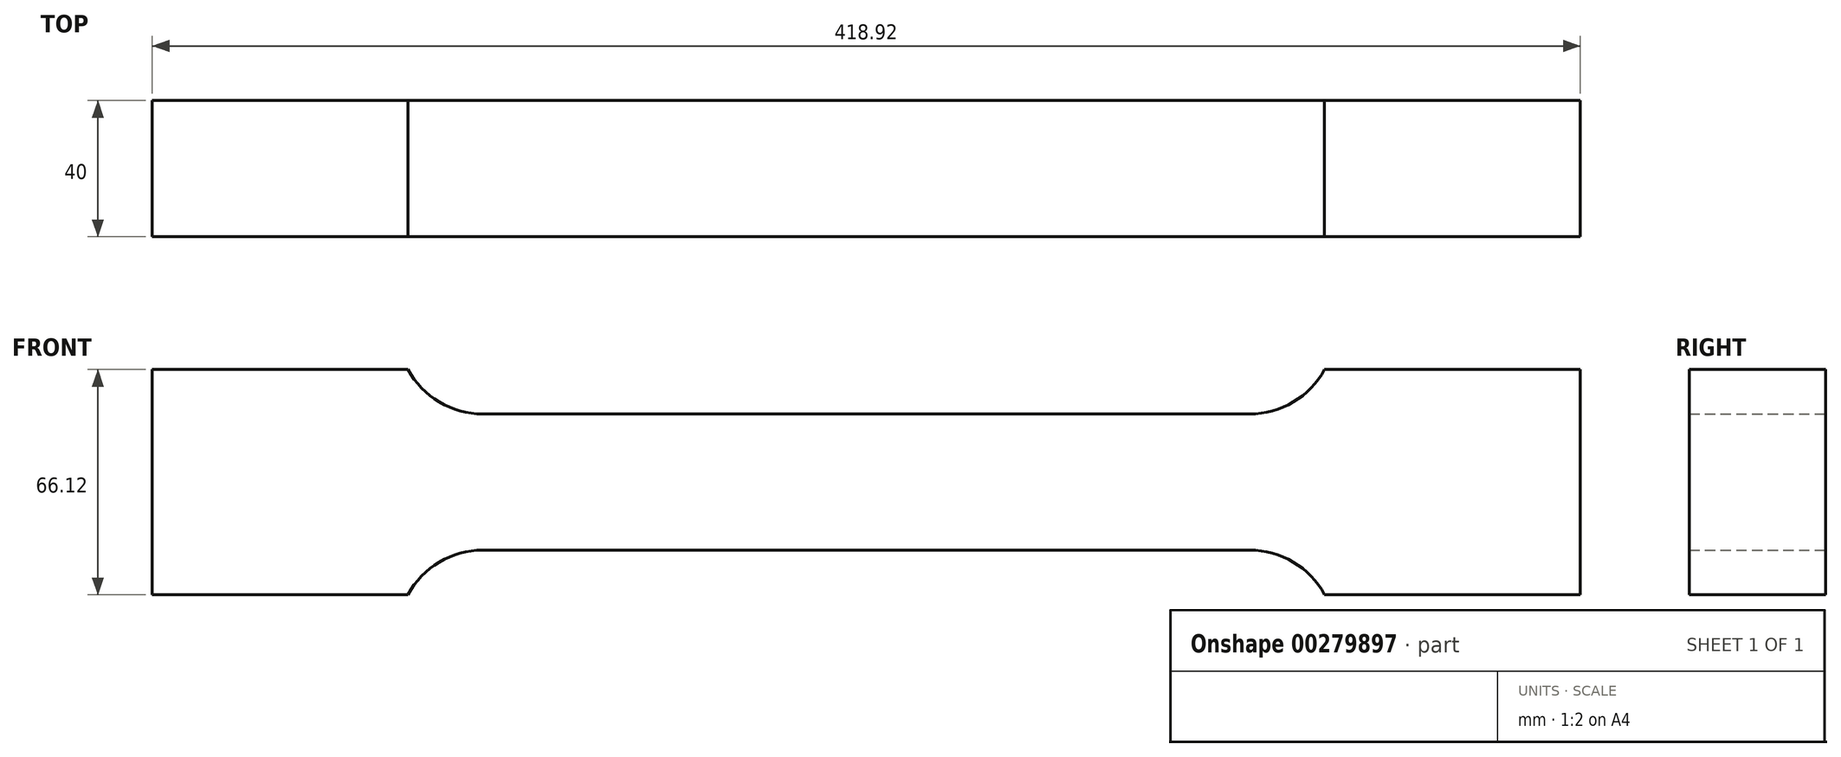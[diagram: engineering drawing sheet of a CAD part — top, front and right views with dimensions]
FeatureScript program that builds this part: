
annotation { "Feature Type Name" : "Feature", "Feature Type Description" : "" }
export const myFeature = defineFeature(function(context is Context, id is Id, definition is map)
    precondition{}
    {
        {
            var Q0;
            Q0=qCreatedBy(makeId("Front.planeOp"),FACE);
            var sketch = newSketch(context, id + "F0", { "sketchPlane" : qUnion([Q0])});
            skLineSegment(sketch, "E0", {"start": v(0, 20) * mm, "end": v(112.5, 20) * mm});
            skLineSegment(sketch, "E1", {"start": v(112.5, 20) * mm, "end": v(56.25, 20) * mm});
            skArc(sketch, "E2", {"start": v(112.5, 20) * mm, "mid": v(125.27, 23.51) * mm, "end": v(134.46, 33.06) * mm});
            skLineSegment(sketch, "E3", {"start": v(134.46, 33.06) * mm, "end": v(209.46, 33.06) * mm});
            skLineSegment(sketch, "E4", {"start": v(209.46, 33.06) * mm, "end": v(209.46, 0) * mm});
            skLineSegment(sketch, "E5.MirrorCS", {"start": v(0, -20) * mm, "end": v(112.5, -20) * mm});
            skLineSegment(sketch, "E6.MirrorCS", {"start": v(209.46, -33.06) * mm, "end": v(209.46, 0) * mm});
            skLineSegment(sketch, "E7.MirrorCS", {"start": v(112.5, -20) * mm, "end": v(56.25, -20) * mm});
            skLineSegment(sketch, "E8.MirrorCS", {"start": v(134.46, -33.06) * mm, "end": v(209.46, -33.06) * mm});
            skArc(sketch, "E9.MirrorCS", {"start": v(112.5, -20) * mm, "mid": v(125.27, -23.51) * mm, "end": v(134.46, -33.06) * mm});
            skArc(sketch, "E10.MirrorCS", {"start": v(-112.5, -20) * mm, "mid": v(-125.27, -23.51) * mm, "end": v(-134.46, -33.06) * mm});
            skLineSegment(sketch, "E11.MirrorCS", {"start": v(-134.46, -33.06) * mm, "end": v(-209.46, -33.06) * mm});
            skLineSegment(sketch, "E12.MirrorCS", {"start": v(-112.5, -20) * mm, "end": v(-56.25, -20) * mm});
            skLineSegment(sketch, "E13.MirrorCS", {"start": v(-209.46, -33.06) * mm, "end": v(-209.46, 0) * mm});
            skArc(sketch, "E14.MirrorCS", {"start": v(-112.5, 20) * mm, "mid": v(-125.27, 23.51) * mm, "end": v(-134.46, 33.06) * mm});
            skLineSegment(sketch, "E15.MirrorCS", {"start": v(-112.5, 20) * mm, "end": v(-56.25, 20) * mm});
            skLineSegment(sketch, "E16.MirrorCS", {"start": v(0, -20) * mm, "end": v(-112.5, -20) * mm});
            skLineSegment(sketch, "E17.MirrorCS", {"start": v(-134.46, 33.06) * mm, "end": v(-209.46, 33.06) * mm});
            skLineSegment(sketch, "E18.MirrorCS", {"start": v(-209.46, 33.06) * mm, "end": v(-209.46, 0) * mm});
            skLineSegment(sketch, "E19.MirrorCS", {"start": v(0, 20) * mm, "end": v(-112.5, 20) * mm});
            skSolve(sketch);
        }
        {
            var Q0;
            {var subQ0=sQuery(id+"F0.wireOp",EDGE,"E0");Q0=makeQuery(id+"F0.imprint","IMPRINT",FACE,{"disambiguationData":[TD([[makeQuery(id+"F0.imprint","IMPRINT",EDGE,{"derivedFrom":subQ0}),-1.0]])]});}
            extrude(context, id + "F1", {"entities" : qUnion([Q0]), "endBound" : BoundingType.SYMMETRIC, "depth" : 40 * mm});
        }
    });
